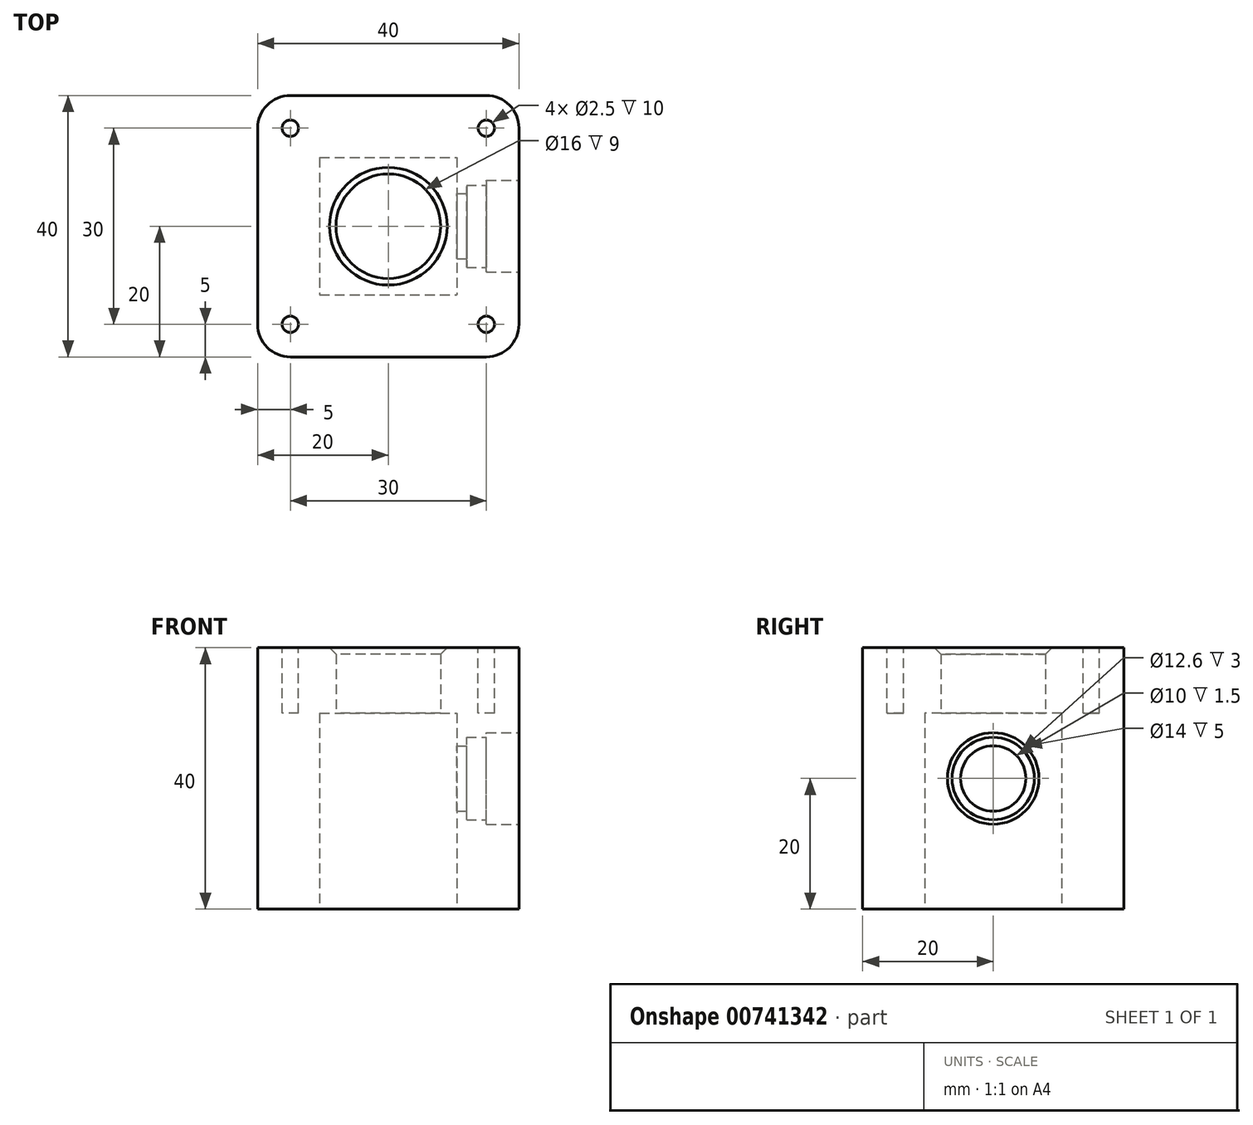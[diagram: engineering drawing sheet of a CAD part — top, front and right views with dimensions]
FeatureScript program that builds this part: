
annotation { "Feature Type Name" : "Feature", "Feature Type Description" : "" }
export const myFeature = defineFeature(function(context is Context, id is Id, definition is map)
    precondition{}
    {
        {
            var Q0;
            Q0=qCreatedBy(makeId("Top.planeOp"),FACE);
            var sketch = newSketch(context, id + "F0", { "sketchPlane" : qUnion([Q0])});
            skLineSegment(sketch, "E0.bottom", {"start": v(-20, 20) * mm, "end": v(20, 20) * mm});
            skLineSegment(sketch, "E0.top", {"start": v(-20, -20) * mm, "end": v(20, -20) * mm});
            skLineSegment(sketch, "E0.left", {"start": v(-20, 20) * mm, "end": v(-20, -20) * mm});
            skLineSegment(sketch, "E0.right", {"start": v(20, 20) * mm, "end": v(20, -20) * mm});
            skCircle(sketch, "E1", {"center": v(0, 0) * mm, "radius": 8 * mm});
            skSolve(sketch);
        }
        {
            var Q0;
            Q0=makeQuery(id+"F0.imprint","IMPRINT",FACE,{"disambiguationData":[TD([[makeQuery(id+"F0.imprint","IMPRINT",EDGE,{"derivedFrom":sQuery(id+"F0.wireOp",EDGE,"E0.bottom")}),-1.0]])]});
            extrude(context, id + "F1", {"entities" : qUnion([Q0]), "depth" : 40 * mm, "offsetDistance" : 25 * mm});
        }
        {
            var Q0;
            Q0=qCreatedBy(makeId("Top.planeOp"),FACE);
            var sketch = newSketch(context, id + "F2", { "sketchPlane" : qUnion([Q0])});
            skLineSegment(sketch, "E2.bottom", {"start": v(-10.5, 10.5) * mm, "end": v(10.5, 10.5) * mm});
            skLineSegment(sketch, "E2.top", {"start": v(-10.5, -10.5) * mm, "end": v(10.5, -10.5) * mm});
            skLineSegment(sketch, "E2.left", {"start": v(-10.5, 10.5) * mm, "end": v(-10.5, -10.5) * mm});
            skLineSegment(sketch, "E2.right", {"start": v(10.5, 10.5) * mm, "end": v(10.5, -10.5) * mm});
            skSolve(sketch);
        }
        {
            var Q0;
            Q0 = qSketchRegion(id + "F2", true);
            extrude(context, id + "F3", {"entities" : qUnion([Q0]), "depth" : 30 * mm, "offsetDistance" : 25 * mm});
        }
        {
            var Q0;
            Q0=makeQuery(id+"F3.opExtrude","SWEPT_BODY",BODY,{"disambiguationData":[OSD([sQuery(id+"F2.wireOp",EDGE,"E2.bottom"),sQuery(id+"F2.wireOp",EDGE,"E2.top"),sQuery(id+"F2.wireOp",EDGE,"E2.left"),sQuery(id+"F2.wireOp",EDGE,"E2.right")])]});
            var Q1;
            Q1=makeQuery(id+"F1.opExtrude","SWEPT_BODY",BODY,{"disambiguationData":[OSD([sQuery(id+"F0.wireOp",EDGE,"E0.bottom"),sQuery(id+"F0.wireOp",EDGE,"E0.top"),sQuery(id+"F0.wireOp",EDGE,"E0.left"),sQuery(id+"F0.wireOp",EDGE,"E0.right"),sQuery(id+"F0.wireOp",EDGE,"E1")])]});
            booleanBodies(context, id + "F4", {"operationType" : BooleanOperationType.SUBTRACTION, "tools" : qUnion([Q0]), "targets" : qUnion([Q1])});
        }
        {
            var Q0;
            Q0=makeQuery(id+"F1.opExtrude","SWEPT_FACE",FACE,{"disambiguationData":[OSD([sQuery(id+"F0.wireOp",EDGE,"E0.right")])]});
            var sketch = newSketch(context, id + "F5", { "sketchPlane" : qUnion([Q0])});
            skCircle(sketch, "E3", {"center": v(0, 20) * mm, "radius": 5 * mm});
            skSolve(sketch);
        }
        {
            var Q0;
            Q0=makeQuery(id+"F5.imprint","IMPRINT",FACE,{"disambiguationData":[TD([[makeQuery(id+"F5.imprint","IMPRINT",EDGE,{"derivedFrom":sQuery(id+"F5.wireOp",EDGE,"E3")}),1.0]])]});
            extrude(context, id + "F6", {"entities" : qUnion([Q0]), "operationType" : NewBodyOperationType.REMOVE, "depth" : -11 * mm, "offsetDistance" : 25 * mm});
        }
        {
            var Q0;
            Q0=makeQuery(id+"F1.opExtrude","SWEPT_FACE",FACE,{"disambiguationData":[OSD([sQuery(id+"F0.wireOp",EDGE,"E0.right")])]});
            var sketch = newSketch(context, id + "F7", { "sketchPlane" : qUnion([Q0])});
            skCircle(sketch, "E4", {"center": v(0, 20) * mm, "radius": 6.3 * mm});
            skSolve(sketch);
        }
        {
            var Q0;
            Q0 = qSketchRegion(id + "F7", true);
            extrude(context, id + "F8", {"entities" : qUnion([Q0]), "operationType" : NewBodyOperationType.REMOVE, "oppositeDirection" : true, "depth" : 8 * mm, "offsetDistance" : 25 * mm});
        }
        {
            var Q0;
            Q0=makeQuery(id+"F1.opExtrude","SWEPT_FACE",FACE,{"disambiguationData":[OSD([sQuery(id+"F0.wireOp",EDGE,"E0.right")])]});
            var sketch = newSketch(context, id + "F9", { "sketchPlane" : qUnion([Q0])});
            skCircle(sketch, "E5", {"center": v(0, 20) * mm, "radius": 7 * mm});
            skSolve(sketch);
        }
        {
            var Q0;
            Q0 = qSketchRegion(id + "F9", true);
            extrude(context, id + "F10", {"entities" : qUnion([Q0]), "operationType" : NewBodyOperationType.REMOVE, "oppositeDirection" : true, "depth" : 5 * mm, "offsetDistance" : 25 * mm});
        }
        {
            var Q0;
            Q0=makeQuery(id+"F1.opExtrude","SWEPT_EDGE",EDGE,{"disambiguationData":[OSD([sQuery(id+"F0.wireOp",EDGE,"E0.bottom"),sQuery(id+"F0.wireOp",EDGE,"E0.right")])]});
            var Q1;
            Q1=makeQuery(id+"F1.opExtrude","SWEPT_EDGE",EDGE,{"disambiguationData":[OSD([sQuery(id+"F0.wireOp",EDGE,"E0.bottom"),sQuery(id+"F0.wireOp",EDGE,"E0.left")])]});
            var Q2;
            Q2=makeQuery(id+"F1.opExtrude","SWEPT_EDGE",EDGE,{"disambiguationData":[OSD([sQuery(id+"F0.wireOp",EDGE,"E0.top"),sQuery(id+"F0.wireOp",EDGE,"E0.left")])]});
            var Q3;
            Q3=makeQuery(id+"F1.opExtrude","SWEPT_EDGE",EDGE,{"disambiguationData":[OSD([sQuery(id+"F0.wireOp",EDGE,"E0.top"),sQuery(id+"F0.wireOp",EDGE,"E0.right")])]});
            fillet(context, id + "F11", {"entities" : qUnion([Q0, Q1, Q2, Q3]), "radius" : 5 * mm, "tangentPropagation" : true, "allowEdgeOverflow" : false});
        }
        {
            var Q0;
            Q0=makeQuery(id+"F1.opExtrude","CAP_EDGE",EDGE,{"disambiguationData":[OSD([sQuery(id+"F0.wireOp",EDGE,"E1")])],"isStart":false});
            chamfer(context, id + "F12", {"entities" : qUnion([Q0]), "width" : 1 * mm, "tangentPropagation" : true});
        }
        {
            var Q0;
            Q0=makeQuery(id+"F1.opExtrude","CAP_FACE",FACE,{"disambiguationData":[OSD([sQuery(id+"F0.wireOp",EDGE,"E0.bottom"),sQuery(id+"F0.wireOp",EDGE,"E0.top"),sQuery(id+"F0.wireOp",EDGE,"E0.left"),sQuery(id+"F0.wireOp",EDGE,"E0.right"),sQuery(id+"F0.wireOp",EDGE,"E1")])],"isStart":false});
            var sketch = newSketch(context, id + "F13", { "sketchPlane" : qUnion([Q0])});
            skCircle(sketch, "E6", {"center": v(-15, 15) * mm, "radius": 1.25 * mm});
            skCircle(sketch, "E7", {"center": v(-15, -15) * mm, "radius": 1.25 * mm});
            skCircle(sketch, "E8", {"center": v(15, -15) * mm, "radius": 1.25 * mm});
            skCircle(sketch, "E9", {"center": v(15, 15) * mm, "radius": 1.25 * mm});
            skSolve(sketch);
        }
        {
            var Q0;
            Q0 = qSketchRegion(id + "F13", true);
            extrude(context, id + "F14", {"entities" : qUnion([Q0]), "operationType" : NewBodyOperationType.REMOVE, "oppositeDirection" : true, "depth" : 10 * mm, "offsetDistance" : 25 * mm});
        }
    });
